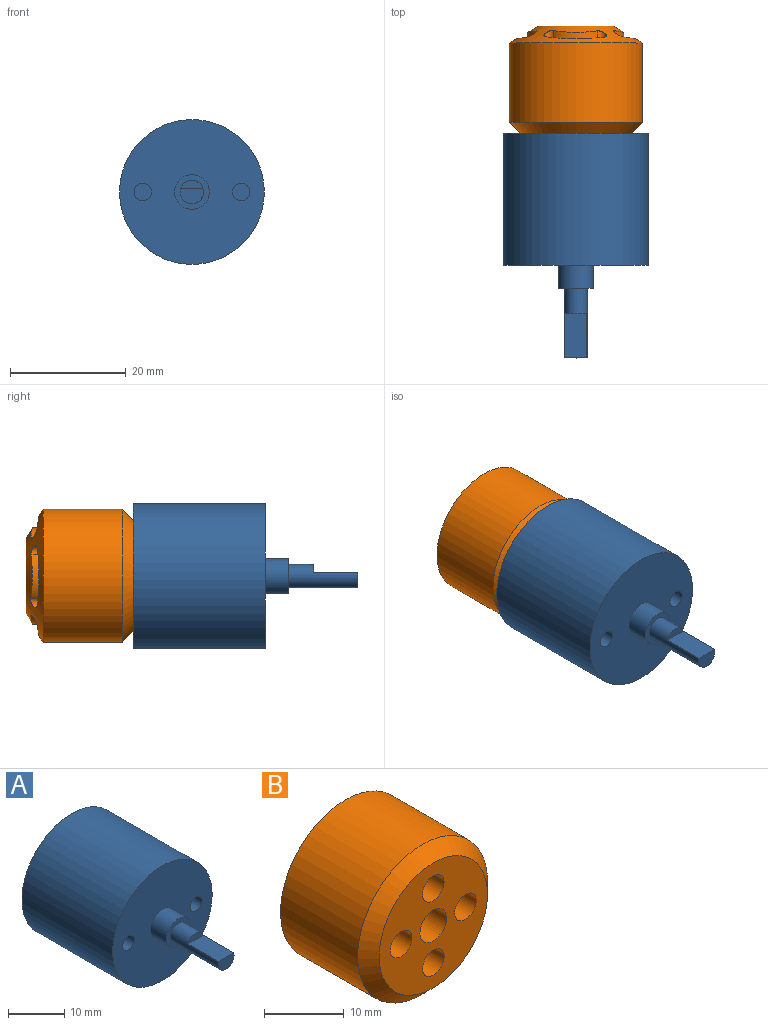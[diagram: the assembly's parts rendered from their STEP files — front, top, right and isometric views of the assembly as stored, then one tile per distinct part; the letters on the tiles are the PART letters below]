
ASSEMBLY  parts=2 mates=1
PART A: 15 faces, bbox 25x38.8x25 mm
  f0: plane 25x25mm, normal (0,-1,0), area 448.5mm2, adj f1,f3,f9,f11
  f1: cylinder r=12.5mm len=25mm, axis (0,1,0), area 1791.5mm2, adj f0,f2
  f2: plane 25x25mm, normal (0,1,0), area 469.1mm2, adj f1,f13
  f3: cylinder r=3mm len=6mm, axis (0,1,0), area 75.4mm2, adj f0,f4
  f4: plane 6x6mm, normal (0,-1,0), area 15.7mm2, adj f3,f5
  f5: cylinder r=2mm len=12mm, axis (0,1,0), area 112.1mm2, adj f4,f6,f7,f8
  f6: plane 4x2.61mm, normal (0,-1,0), area 8.7mm2, adj f5,f8
  f7: plane 3.81x1.39mm, normal (0,-1,0), area 3.9mm2, adj f5,f8
  f8: plane 7.67x3.81mm, normal (0,0,1), area 29.2mm2, adj f5,f6,f7
  f9: cylinder r=1.5mm len=12.7mm, axis (0,-1,0), area 119.7mm2, adj f0,f10
  f10: plane 3x3mm, normal (0,-1,0), area 7.1mm2, adj f9
  f11: cylinder r=1.5mm len=12.7mm, axis (0,-1,0), area 119.7mm2, adj f0,f12
  f12: plane 3x3mm, normal (0,-1,0), area 7.1mm2, adj f11
  f13: cylinder r=2.64mm len=5.27mm, axis (0,1,0), area 42.1mm2, adj f2,f14
  f14: plane 5.27x5.27mm, normal (0,1,0), area 21.8mm2, adj f13
PART B: 35 faces, bbox 23x18.5x23 mm
  f0: plane 12.84x12.84mm, normal (0,1,0), area 129.5mm2, adj f24
  f1: cylinder r=11.5mm len=23mm, axis (0,-1,0), area 987.2mm2, adj f23,f24
  f2: plane 19.19x19.19mm, normal (0,-1,0), area 225.7mm2, adj f23,f25,f27,f29,f31,f33
  f3: cylinder r=0.99mm len=1.72mm, axis (0,1,0), area 3.2mm2, adj f4,f6,f7,f24
  f4: cylinder r=5.72mm len=7.74mm, axis (0,1,0), area 13.2mm2, adj f3,f5,f7,f24
  f5: cylinder r=0.97mm len=1.75mm, axis (0,1,0), area 3.6mm2, adj f4,f6,f7,f24
  f6: cylinder r=7.64mm len=10.34mm, axis (0,1,0), area 5.1mm2, adj f3,f5,f7,f24
  f7: plane 10.75x3.72mm, normal (0,1,0), area 21.4mm2, adj f3,f4,f5,f6
  f8: cylinder r=0.99mm len=1.72mm, axis (0,1,0), area 3.2mm2, adj f9,f11,f12,f24
  f9: cylinder r=5.72mm len=7.74mm, axis (0,1,0), area 13.2mm2, adj f8,f10,f12,f24
  f10: cylinder r=0.97mm len=1.75mm, axis (0,1,0), area 3.6mm2, adj f9,f11,f12,f24
  f11: cylinder r=7.64mm len=10.34mm, axis (0,1,0), area 5.1mm2, adj f8,f10,f12,f24
  f12: plane 10.75x3.72mm, normal (0,1,0), area 21.4mm2, adj f8,f9,f10,f11
  f13: cylinder r=0.99mm len=1.72mm, axis (0,1,0), area 3.2mm2, adj f14,f16,f17,f24
  f14: cylinder r=5.72mm len=7.74mm, axis (0,1,0), area 13.2mm2, adj f13,f15,f17,f24
  f15: cylinder r=0.97mm len=1.75mm, axis (0,1,0), area 3.6mm2, adj f14,f16,f17,f24
  f16: cylinder r=7.64mm len=10.34mm, axis (0,1,0), area 5.1mm2, adj f13,f15,f17,f24
  f17: plane 10.75x3.72mm, normal (0,1,0), area 21.4mm2, adj f13,f14,f15,f16
  f18: cylinder r=0.99mm len=1.72mm, axis (0,1,0), area 3.2mm2, adj f19,f21,f22,f24
  f19: cylinder r=5.72mm len=7.74mm, axis (0,1,0), area 13.2mm2, adj f18,f20,f22,f24
  f20: cylinder r=0.97mm len=1.75mm, axis (0,1,0), area 3.6mm2, adj f19,f21,f22,f24
  f21: cylinder r=7.64mm len=10.34mm, axis (0,1,0), area 5.1mm2, adj f18,f20,f22,f24
  f22: plane 10.75x3.72mm, normal (0,1,0), area 21.4mm2, adj f18,f19,f20,f21
  f23: cone r=11.5mm half-angle=45deg, axis (0,1,0), area 178.5mm2, adj f1,f2
  f24: cone r=6.42mm half-angle=60deg, axis (0,-1,0), area 231.3mm2, adj f0,f1,f3,f4,f5,f6,f8,f9
  f25: cylinder r=2.37mm len=4.74mm, axis (0,-1,0), area 56.7mm2, adj f2,f26
  f26: plane 4.74x4.74mm, normal (0,-1,0), area 17.6mm2, adj f25
  f27: cylinder r=1.91mm len=3.82mm, axis (0,-1,0), area 45.8mm2, adj f2,f28
  f28: plane 3.82x3.82mm, normal (0,-1,0), area 11.5mm2, adj f27
  f29: cylinder r=1.91mm len=3.82mm, axis (0,-1,0), area 45.8mm2, adj f2,f30
  f30: plane 3.82x3.82mm, normal (0,-1,0), area 11.5mm2, adj f29
  f31: cylinder r=1.91mm len=3.82mm, axis (0,-1,0), area 45.8mm2, adj f2,f32
  f32: plane 3.82x3.82mm, normal (0,-1,0), area 11.5mm2, adj f31
  f33: cylinder r=1.91mm len=3.82mm, axis (0,-1,0), area 45.8mm2, adj f2,f34
  f34: plane 3.82x3.82mm, normal (0,-1,0), area 11.5mm2, adj f33
PLACE A t=(-40.99,-35.09,-14.15)mm
PLACE B t=(-82.5,-54.1,32.69)mm
MATE fastened A.f1 <-> B.f1  axis (0,1,0) through (-82.5,-35.09,32.69)mm
